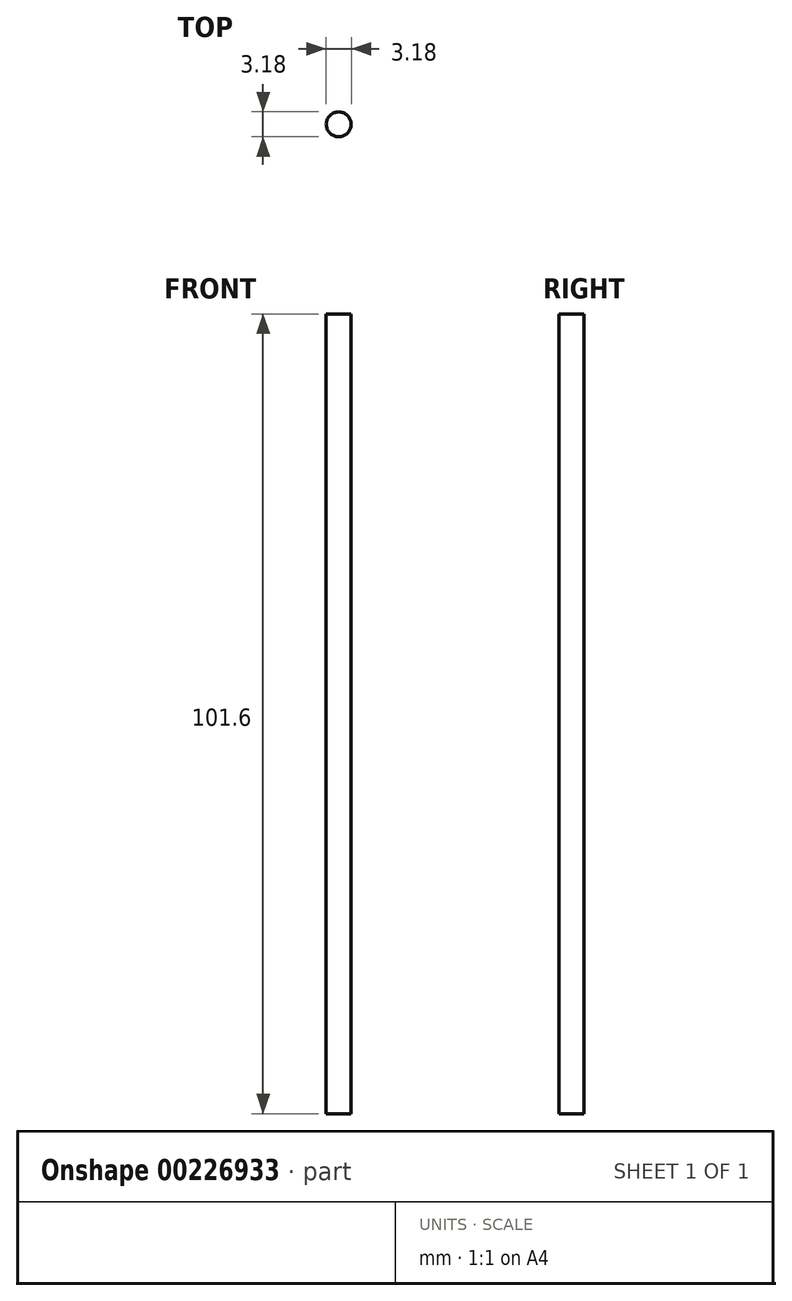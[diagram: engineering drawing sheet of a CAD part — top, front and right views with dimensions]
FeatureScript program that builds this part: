
annotation { "Feature Type Name" : "Feature", "Feature Type Description" : "" }
export const myFeature = defineFeature(function(context is Context, id is Id, definition is map)
    precondition{}
    {
        {
            var Q0;
            Q0=qCreatedBy(makeId("Top.planeOp"),FACE);
            var sketch = newSketch(context, id + "F0", { "sketchPlane" : qUnion([Q0])});
            skCircle(sketch, "E0", {"center": v(-29.95, 19.54) * mm, "radius": 1.59 * mm});
            skSolve(sketch);
        }
        {
            var Q0;
            Q0 = qSketchRegion(id + "F0", true);
            extrude(context, id + "F1", {"entities" : qUnion([Q0]), "depth" : 101.6 * mm});
        }
    });
